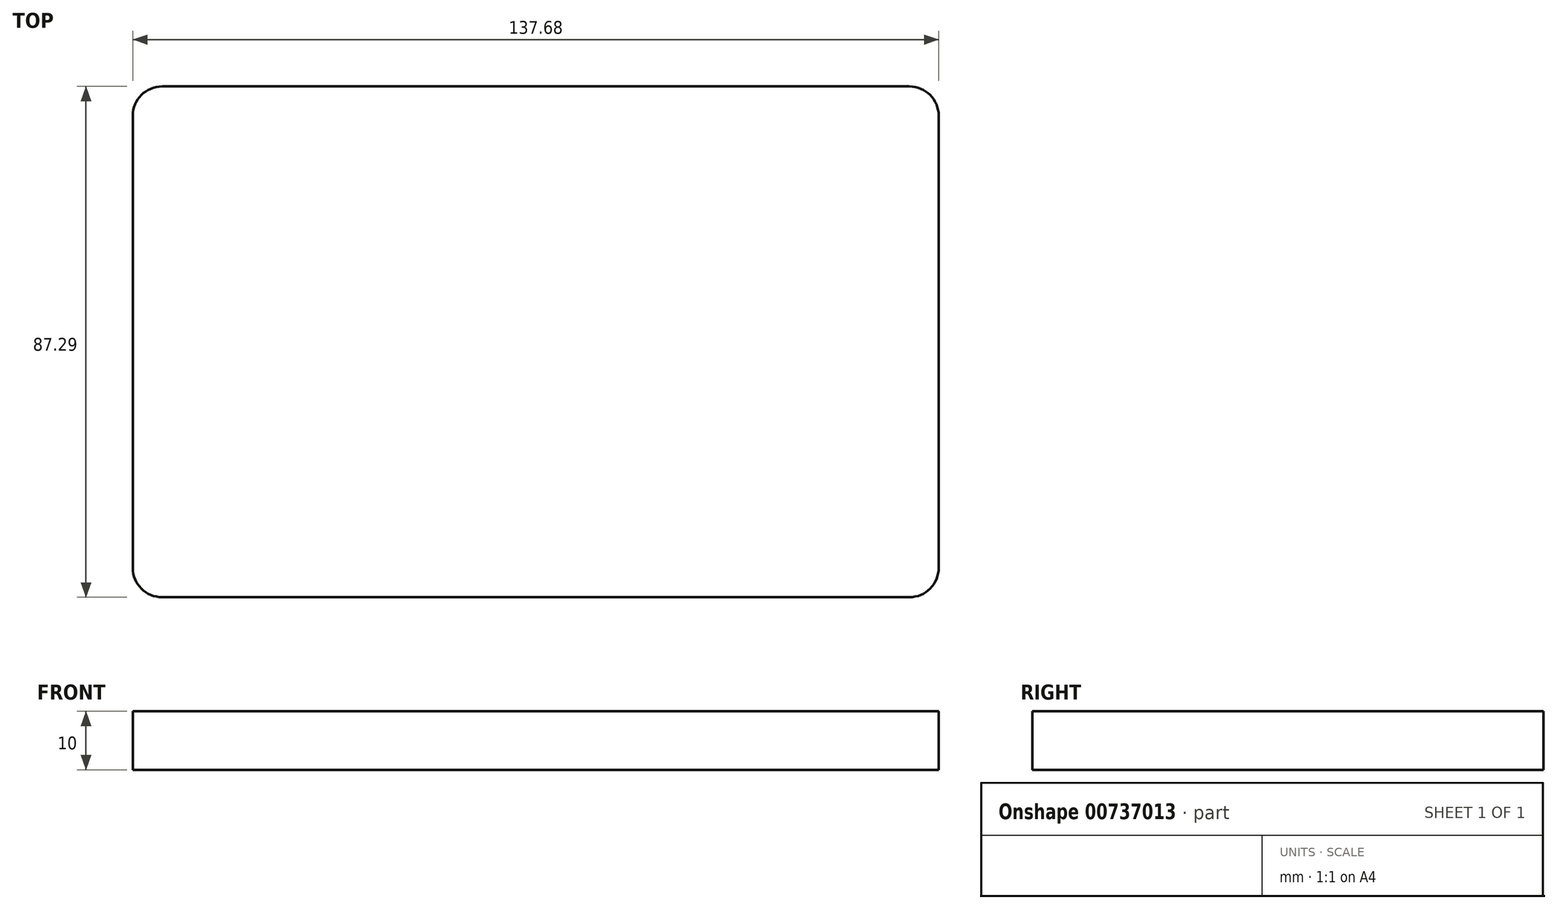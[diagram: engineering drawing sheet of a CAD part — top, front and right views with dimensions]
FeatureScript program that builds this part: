
annotation { "Feature Type Name" : "Feature", "Feature Type Description" : "" }
export const myFeature = defineFeature(function(context is Context, id is Id, definition is map)
    precondition{}
    {
        {
            var Q0;
            Q0=qCreatedBy(makeId("Top.planeOp"),FACE);
            var sketch = newSketch(context, id + "F0", { "sketchPlane" : qUnion([Q0])});
            skLineSegment(sketch, "E0.bottom", {"start": v(-64.73, 61.28) * mm, "end": v(62.95, 61.28) * mm});
            skLineSegment(sketch, "E0.top", {"start": v(-64.73, -26.01) * mm, "end": v(62.95, -26.01) * mm});
            skLineSegment(sketch, "E0.left", {"start": v(-69.73, 56.28) * mm, "end": v(-69.73, -21.01) * mm});
            skLineSegment(sketch, "E0.right", {"start": v(67.95, 56.28) * mm, "end": v(67.95, -21.01) * mm});
            skPoint(sketch, "E1.visualSharp", {"position": v(-69.73, -26.01) * mm});
            skArc(sketch, "E1.filletArc", {"start": v(-69.73, -21.01) * mm, "mid": v(-68.27, -24.55) * mm, "end": v(-64.73, -26.01) * mm});
            skPoint(sketch, "E2.visualSharp", {"position": v(-69.73, 61.28) * mm});
            skArc(sketch, "E2.filletArc", {"start": v(-64.73, 61.28) * mm, "mid": v(-68.27, 59.82) * mm, "end": v(-69.73, 56.28) * mm});
            skPoint(sketch, "E3.visualSharp", {"position": v(67.95, 61.28) * mm});
            skArc(sketch, "E3.filletArc", {"start": v(67.95, 56.28) * mm, "mid": v(66.48, 59.82) * mm, "end": v(62.95, 61.28) * mm});
            skPoint(sketch, "E4.visualSharp", {"position": v(67.95, -26.01) * mm});
            skArc(sketch, "E4.filletArc", {"start": v(62.95, -26.01) * mm, "mid": v(66.48, -24.55) * mm, "end": v(67.95, -21.01) * mm});
            skSolve(sketch);
        }
        {
            var Q0;
            Q0=makeQuery(id+"F0.imprint","IMPRINT",FACE,{"disambiguationData":[TD([[makeQuery(id+"F0.imprint","IMPRINT",EDGE,{"derivedFrom":sQuery(id+"F0.wireOp",EDGE,"E0.bottom")}),-1.0]])]});
            extrude(context, id + "F1", {"entities" : qUnion([Q0]), "depth" : 10 * mm, "offsetDistance" : 25 * mm});
        }
    });
